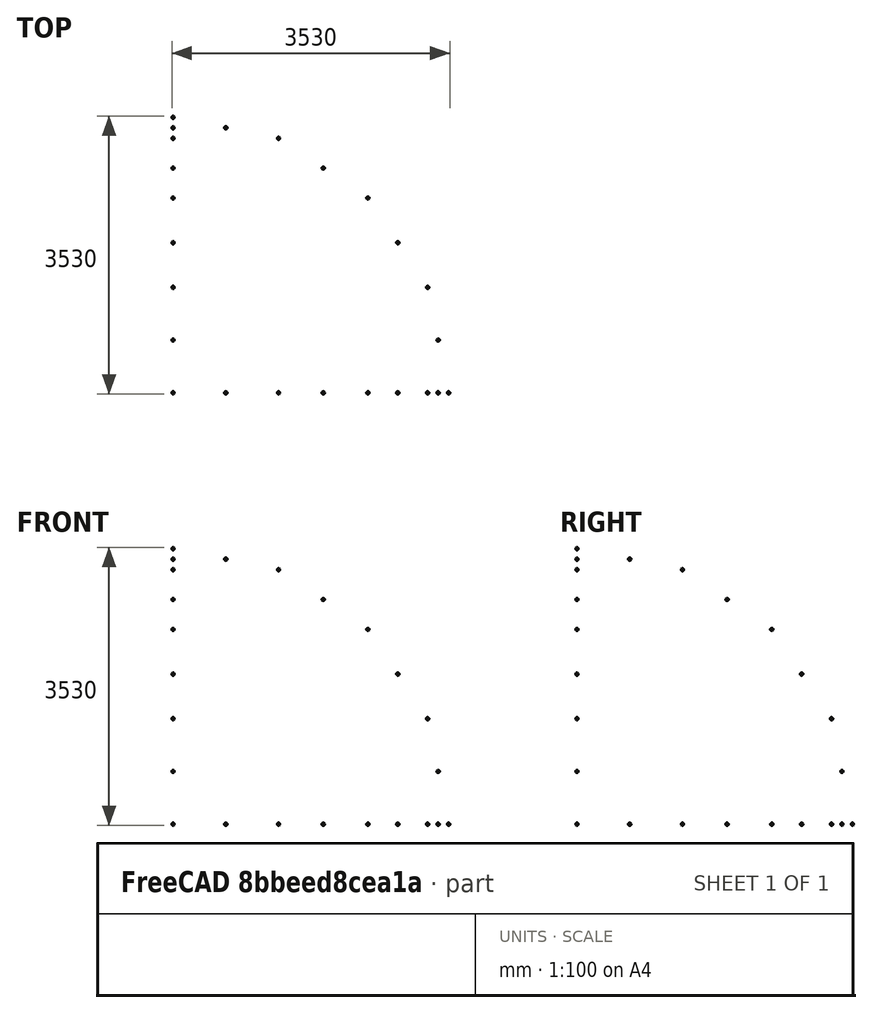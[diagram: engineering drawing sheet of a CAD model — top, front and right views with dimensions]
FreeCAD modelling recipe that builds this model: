
FCSTD DOCUMENT  (FreeCAD 0.20R29603 (Git))
Label: oi_pointing
License: All rights reserved
LicenseURL: http://en.wikipedia.org/wiki/All_rights_reserved
objects: Part::Sphere×25, Part::Part2DObjectPython×20
note: 45 computed .brp shape members not serialized (recipe doc carries the construction recipe); baked Part::Feature solids carry a one-line shape summary decoded from their .brp

FEATURE [Part::Part2DObjectPython] Line  # Draft 2D object (typed FeaturePython)
  Area = 0
  ChamferSize = 0
  Closed = false
  End = (3233.58,0,1339.39)
  FilletRadius = 0
  Length = 1365.63
  MakeFace = false
  Points = (2) [(3500,0,0),(3233.58,0,1339.39)]
  Start = (3500,0,0)
  Subdivisions = 0
FEATURE [Part::Part2DObjectPython] Line002  # Draft 2D object (typed FeaturePython)
  Area = 0
  ChamferSize = 0
  Closed = false
  End = (3233.58,1339.39,0)
  FilletRadius = 0
  Length = 1365.63
  MakeFace = false
  Points = (2) [(3500,0,0),(3233.58,1339.39,0)]
  Start = (3500,0,0)
  Subdivisions = 0
FEATURE [Part::Part2DObjectPython] Line003  # Draft 2D object (typed FeaturePython)
  Area = 0
  ChamferSize = 0
  Closed = false
  End = (2987.44,1237.44,1339.39)
  FilletRadius = 0
  Length = 1261.68
  MakeFace = false
  Points = (2) [(3233.58,0,1339.39),(2987.44,1237.44,1339.39)]
  Start = (3233.58,0,1339.39)
  Subdivisions = 0
FEATURE [Part::Part2DObjectPython] Line004  # Draft 2D object (typed FeaturePython)
  Area = 0
  ChamferSize = 0
  Closed = false
  End = (2286.49,947.093,2474.87)
  FilletRadius = 0
  Length = 965.648
  MakeFace = false
  Points = (2) [(2474.87,0,2474.87),(2286.49,947.093,2474.87)]
  Start = (2474.87,0,2474.87)
  Subdivisions = 0
FEATURE [Part::Part2DObjectPython] Line005  # Draft 2D object (typed FeaturePython)
  Area = 0
  ChamferSize = 0
  Closed = false
  End = (1237.44,512.563,3233.58)
  FilletRadius = 0
  Length = 522.605
  MakeFace = false
  Points = (2) [(1339.39,0,3233.58),(1237.44,512.563,3233.58)]
  Start = (1339.39,0,3233.58)
  Subdivisions = 0
FEATURE [Part::Part2DObjectPython] Line006  # Draft 2D object (typed FeaturePython)
  Area = 0
  ChamferSize = 0
  Closed = false
  End = (0.0092388,0.00382683,3500)
  FilletRadius = 0
  Length = 0.00390181
  MakeFace = false
  Points = (2) [(0.01,0,3500),(0.0092388,0.00382683,3500)]
  Start = (0.01,0,3500)
  Subdivisions = 0
FEATURE [Part::Part2DObjectPython] Line007  # Draft 2D object (typed FeaturePython)
  Area = 0
  ChamferSize = 0
  Closed = false
  End = (2474.87,0,2474.87)
  FilletRadius = 0
  Length = 1365.63
  MakeFace = false
  Placement = pos=(0,0,0) rot=(0,-1,0;0.392699rad)
  Points = (2) [(3500,0,2.27374e-13),(3233.58,0,1339.39)]
  Start = (3233.58,0,1339.39)
  Subdivisions = 0
FEATURE [Part::Part2DObjectPython] Line008  # Draft 2D object (typed FeaturePython)
  Area = 0
  ChamferSize = 0
  Closed = false
  End = (-1.3642e-12,0,3500)
  FilletRadius = 0
  Length = 1365.63
  MakeFace = false
  Placement = pos=(0,0,0) rot=(0,-1,0;1.1781rad)
  Points = (2) [(3500,0,-4.54747e-13),(3233.58,0,1339.39)]
  Start = (1339.39,0,3233.58)
  Subdivisions = 0
FEATURE [Part::Part2DObjectPython] Line009  # Draft 2D object (typed FeaturePython)
  Area = 0
  ChamferSize = 0
  Closed = false
  End = (1339.39,0,3233.58)
  FilletRadius = 0
  Length = 1365.63
  MakeFace = false
  Placement = pos=(0,0,0) rot=(0,-1,0;0.785398rad)
  Points = (2) [(3500,0,-9.09495e-13),(3233.58,0,1339.39)]
  Start = (2474.87,0,2474.87)
  Subdivisions = 0
FEATURE [Part::Part2DObjectPython] Line010  # Draft 2D object (typed FeaturePython)
  Area = 0
  ChamferSize = 0
  Closed = false
  End = (-1.7053e-12,-2.5011e-12,3500)
  FilletRadius = 0
  Length = 3500
  MakeFace = true
  Placement = pos=(0,0,0) rot=(0.799257,0.125953,0.587643;1.11975rad)
  Points = (2) [(0,0,0),(530.542,2663.76,2207.47)]
  Start = (0,0,0)
  Subdivisions = 0
FEATURE [Part::Part2DObjectPython] Line011  # Draft 2D object (typed FeaturePython)
  Area = 0
  ChamferSize = 0
  Closed = false
  End = (3500,-6.821e-13,0)
  FilletRadius = 0
  Length = 3500
  MakeFace = true
  Placement = pos=(0,0,0) rot=(0.799257,0.125953,0.587643;1.11975rad)
  Points = (2) [(0,0,0),(2786.9,-1652.3,1324.04)]
  Start = (0,0,0)
  Subdivisions = 0
FEATURE [Part::Part2DObjectPython] Line012  # Draft 2D object (typed FeaturePython)
  Area = 0
  ChamferSize = 0
  Closed = false
  End = (2474.87,2474.87,0)
  FilletRadius = 0
  Length = 1365.63
  MakeFace = false
  Placement = pos=(0,0,0) rot=(0,0,1;0.392699rad)
  Points = (2) [(3500,0,0),(3233.58,1339.39,0)]
  Start = (3233.58,1339.39,0)
  Subdivisions = 0
FEATURE [Part::Part2DObjectPython] Line013  # Draft 2D object (typed FeaturePython)
  Area = 0
  ChamferSize = 0
  Closed = false
  End = (1339.39,3233.58,0)
  FilletRadius = 0
  Length = 1365.63
  MakeFace = false
  Placement = pos=(0,0,0) rot=(0,0,1;0.785398rad)
  Points = (2) [(3500,0,0),(3233.58,1339.39,0)]
  Start = (2474.87,2474.87,0)
  Subdivisions = 0
FEATURE [Part::Part2DObjectPython] Line014  # Draft 2D object (typed FeaturePython)
  Area = 0
  ChamferSize = 0
  Closed = false
  End = (-3.4106e-12,3500,0)
  FilletRadius = 0
  Length = 1365.63
  MakeFace = false
  Placement = pos=(0,0,0) rot=(0,0,1;1.1781rad)
  Points = (2) [(3500,0,0),(3233.58,1339.39,0)]
  Start = (1339.39,3233.58,0)
  Subdivisions = 0
FEATURE [Part::Part2DObjectPython] Line015  # Draft 2D object (typed FeaturePython)
  Area = 0
  ChamferSize = 0
  Closed = false
  End = (-6.1391e-12,3500,-1.5348e-12)
  FilletRadius = 0
  Length = 3500
  MakeFace = true
  Placement = pos=(0,0,0) rot=(0.23465,0.959688,0.154721;0.514623rad)
  Points = (2) [(0,0,0),(368.626,3464.19,-336.926)]
  Start = (0,0,0)
  Subdivisions = 0
FEATURE [Part::Part2DObjectPython] Line016  # Draft 2D object (typed FeaturePython)
  Area = 0
  ChamferSize = 0
  Closed = false
  End = (-1.334e-12,-9.095e-13,3500)
  FilletRadius = 0
  Length = 1365.63
  MakeFace = false
  Placement = pos=(0,0,0) rot=(0.485653,-0.485653,0.726831;1.88458rad)
  Points = (2) [(3500,2.66162e-13,-9.09495e-13),(3233.58,-2.59867e-14,1339.39)]
  Start = (-4.5711e-12,1339.39,3233.58)
  Subdivisions = 0
FEATURE [Part::Part2DObjectPython] Line017  # Draft 2D object (typed FeaturePython)
  Area = 0
  ChamferSize = 0
  Closed = false
  End = (-2.261e-12,1339.39,3233.58)
  FilletRadius = 0
  Length = 1365.63
  MakeFace = false
  Placement = pos=(0,0,0) rot=(0.357407,-0.357407,0.862856;1.71777rad)
  Points = (2) [(3500,1.6026e-13,1.81899e-12),(3233.58,1.30286e-13,1339.39)]
  Start = (-3.3201e-12,2474.87,2474.87)
  Subdivisions = 0
FEATURE [Part::Part2DObjectPython] Line018  # Draft 2D object (typed FeaturePython)
  Area = 0
  ChamferSize = 0
  Closed = false
  End = (-5.3986e-12,2474.87,2474.87)
  FilletRadius = 0
  Length = 1365.63
  MakeFace = false
  Placement = pos=(0,0,0) rot=(0.19148,-0.19148,0.962637;1.60887rad)
  Points = (2) [(3500,1.24079e-13,2.27374e-13),(3233.58,1.09381e-13,1339.39)]
  Start = (-6.9822e-12,3233.58,1339.39)
  Subdivisions = 0
FEATURE [Part::Part2DObjectPython] Line019  # Draft 2D object (typed FeaturePython)
  Area = 0
  ChamferSize = 0
  Closed = false
  End = (-3.59e-12,3233.58,1339.39)
  FilletRadius = 0
  Length = 1365.63
  MakeFace = false
  Placement = pos=(0,0,0) rot=(0,0,1;1.5708rad)
  Points = (2) [(3500,0,0),(3233.58,0,1339.39)]
  Start = (-3.8858e-12,3500,0)
  Subdivisions = 0
FEATURE [Part::Sphere] Sphere  label="Сфера"
  Angle1 = -90
  Angle2 = 90
  Angle3 = 360
  AttacherType = Attacher::AttachEngine3D
  Placement = pos=(3500,0,0) rot=(0,0,1;0rad)
  Radius = 15
FEATURE [Part::Sphere] Sphere001  label="Сфера001"
  Angle1 = -90
  Angle2 = 90
  Angle3 = 360
  AttacherType = Attacher::AttachEngine3D
  Radius = 15
FEATURE [Part::Sphere] Sphere002  label="Сфера002"
  Angle1 = -90
  Angle2 = 90
  Angle3 = 360
  AttacherType = Attacher::AttachEngine3D
  Placement = pos=(-1.1369e-12,-1.3642e-12,3500) rot=(0,0,1;0rad)
  Radius = 15
FEATURE [Part::Sphere] Sphere003  label="Сфера003"
  Angle1 = -90
  Angle2 = 90
  Angle3 = 360
  AttacherType = Attacher::AttachEngine3D
  Placement = pos=(1339.39,-1.3642e-12,3233.58) rot=(0,0,1;0rad)
  Radius = 15
FEATURE [Part::Sphere] Sphere004  label="Сфера004"
  Angle1 = -90
  Angle2 = 90
  Angle3 = 360
  AttacherType = Attacher::AttachEngine3D
  Placement = pos=(2474.87,-1.3642e-12,2474.87) rot=(0,0,1;0rad)
  Radius = 15
FEATURE [Part::Sphere] Sphere005  label="Сфера005"
  Angle1 = -90
  Angle2 = 90
  Angle3 = 360
  AttacherType = Attacher::AttachEngine3D
  Placement = pos=(3233.58,-1.3642e-12,1339.39) rot=(0,0,1;0rad)
  Radius = 15
FEATURE [Part::Sphere] Sphere006  label="Сфера006"
  Angle1 = -90
  Angle2 = 90
  Angle3 = 360
  AttacherType = Attacher::AttachEngine3D
  Placement = pos=(4.547e-12,3500,3.183e-12) rot=(0,0,1;0rad)
  Radius = 15
FEATURE [Part::Sphere] Sphere007  label="Сфера007"
  Angle1 = -90
  Angle2 = 90
  Angle3 = 360
  AttacherType = Attacher::AttachEngine3D
  Placement = pos=(4.9019e-12,3233.58,1339.39) rot=(0,0,1;0rad)
  Radius = 15
FEATURE [Part::Sphere] Sphere008  label="Сфера008"
  Angle1 = -90
  Angle2 = 90
  Angle3 = 360
  AttacherType = Attacher::AttachEngine3D
  Placement = pos=(6.1161e-12,2474.87,2474.87) rot=(0,0,1;0rad)
  Radius = 15
FEATURE [Part::Sphere] Sphere009  label="Сфера009"
  Angle1 = -90
  Angle2 = 90
  Angle3 = 360
  AttacherType = Attacher::AttachEngine3D
  Placement = pos=(8.746e-12,1339.39,3233.58) rot=(0,0,1;0rad)
  Radius = 15
FEATURE [Part::Sphere] Sphere010  label="Сфера010"
  Angle1 = -90
  Angle2 = 90
  Angle3 = 360
  AttacherType = Attacher::AttachEngine3D
  Placement = pos=(1339.39,3233.58,-2.728e-12) rot=(0,0,1;0rad)
  Radius = 15
FEATURE [Part::Sphere] Sphere011  label="Сфера011"
  Angle1 = -90
  Angle2 = 90
  Angle3 = 360
  AttacherType = Attacher::AttachEngine3D
  Placement = pos=(2474.87,2474.87,-2.728e-12) rot=(0,0,1;0rad)
  Radius = 15
FEATURE [Part::Sphere] Sphere012  label="Сфера012"
  Angle1 = -90
  Angle2 = 90
  Angle3 = 360
  AttacherType = Attacher::AttachEngine3D
  Placement = pos=(3233.58,1339.39,-2.728e-12) rot=(0,0,1;0rad)
  Radius = 15
FEATURE [Part::Sphere] Sphere013  label="Сфера013"
  Angle1 = -90
  Angle2 = 90
  Angle3 = 360
  AttacherType = Attacher::AttachEngine3D
  Placement = pos=(3366.79,669.696,0) rot=(0,0,1;0rad)
  Radius = 15
FEATURE [Part::Sphere] Sphere014  label="Сфера014"
  Angle1 = -90
  Angle2 = 90
  Angle3 = 360
  AttacherType = Attacher::AttachEngine3D
  Placement = pos=(2854.23,1907.13,0) rot=(0,0,1;0rad)
  Radius = 15
FEATURE [Part::Sphere] Sphere015  label="Сфера015"
  Angle1 = -90
  Angle2 = 90
  Angle3 = 360
  AttacherType = Attacher::AttachEngine3D
  Placement = pos=(1907.13,2854.23,0) rot=(0,0,1;0rad)
  Radius = 15
FEATURE [Part::Sphere] Sphere016  label="Сфера016"
  Angle1 = -90
  Angle2 = 90
  Angle3 = 360
  AttacherType = Attacher::AttachEngine3D
  Placement = pos=(669.696,3366.79,0) rot=(0,0,1;0rad)
  Radius = 15
FEATURE [Part::Sphere] Sphere017  label="Сфера017"
  Angle1 = -90
  Angle2 = 90
  Angle3 = 360
  AttacherType = Attacher::AttachEngine3D
  Placement = pos=(-4.3201e-12,3366.79,669.696) rot=(0,0,1;0rad)
  Radius = 15
FEATURE [Part::Sphere] Sphere018  label="Сфера018"
  Angle1 = -90
  Angle2 = 90
  Angle3 = 360
  AttacherType = Attacher::AttachEngine3D
  Placement = pos=(-4.664e-12,2854.23,1907.13) rot=(0,0,1;0rad)
  Radius = 15
FEATURE [Part::Sphere] Sphere019  label="Сфера019"
  Angle1 = -90
  Angle2 = 90
  Angle3 = 360
  AttacherType = Attacher::AttachEngine3D
  Placement = pos=(-2.188e-12,1907.13,2854.23) rot=(0,0,1;0rad)
  Radius = 15
FEATURE [Part::Sphere] Sphere020  label="Сфера020"
  Angle1 = -90
  Angle2 = 90
  Angle3 = 360
  AttacherType = Attacher::AttachEngine3D
  Placement = pos=(-1.925e-12,669.696,3366.79) rot=(0,0,1;0rad)
  Radius = 15
FEATURE [Part::Sphere] Sphere021  label="Сфера021"
  Angle1 = -90
  Angle2 = 90
  Angle3 = 360
  AttacherType = Attacher::AttachEngine3D
  Placement = pos=(669.696,-1.14e-13,3366.79) rot=(0,0,1;0rad)
  Radius = 15
FEATURE [Part::Sphere] Sphere022  label="Сфера022"
  Angle1 = -90
  Angle2 = 90
  Angle3 = 360
  AttacherType = Attacher::AttachEngine3D
  Placement = pos=(1907.13,-1.14e-13,2854.23) rot=(0,0,1;0rad)
  Radius = 15
FEATURE [Part::Sphere] Sphere023  label="Сфера023"
  Angle1 = -90
  Angle2 = 90
  Angle3 = 360
  AttacherType = Attacher::AttachEngine3D
  Placement = pos=(2854.23,-1.14e-13,1907.13) rot=(0,0,1;0rad)
  Radius = 15
FEATURE [Part::Sphere] Sphere024  label="Сфера024"
  Angle1 = -90
  Angle2 = 90
  Angle3 = 360
  AttacherType = Attacher::AttachEngine3D
  Placement = pos=(3366.79,-1.14e-13,669.696) rot=(0,0,1;0rad)
  Radius = 15
FEATURE [Part::Part2DObjectPython] Line020  # Draft 2D object (typed FeaturePython)
  Area = 0
  ChamferSize = 0
  Closed = false
  End = (3366.79,669.696,2.274e-13)
  FilletRadius = 0
  Length = 3432.75
  MakeFace = true
  Placement = pos=(0,0,0) rot=(0.187053,0.451587,0.872399;2.44808rad)
  Points = (2) [(0,0,0),(-1907.13,-1647.89,2330.47)]
  Start = (0,0,0)
  Subdivisions = 0
